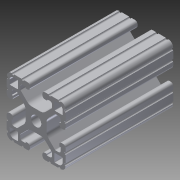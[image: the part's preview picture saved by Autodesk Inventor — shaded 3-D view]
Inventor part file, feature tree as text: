
AUTODESK INVENTOR PART (.ipt)
format: ipt  version: 2013 (Build 170138000, 138)  size: 303,616 bytes
history: native  units: in
note: dims shown in document units (in); Inventor stores cm internally (conversion verified against a paired STEP export)
features: extrude x1, sketch x1
ambient origin geometry x8: Origin, YZ Plane, XZ Plane, XY Plane, X Axis, Y Axis, Z Axis, Center Point
bodies: Solid1 (feature_tree)
feature tree (2):
  extrude  "Extrusion1"  [1 undecoded]
  sketch  "Sketch1"  dims[d0=2.75in d1=0.0in]
note: 1 required parameter value undecoded (feature->parameter linkage not recoverable at this tier; creation-order binding heuristic only, values carry confidence <= 0.55)
